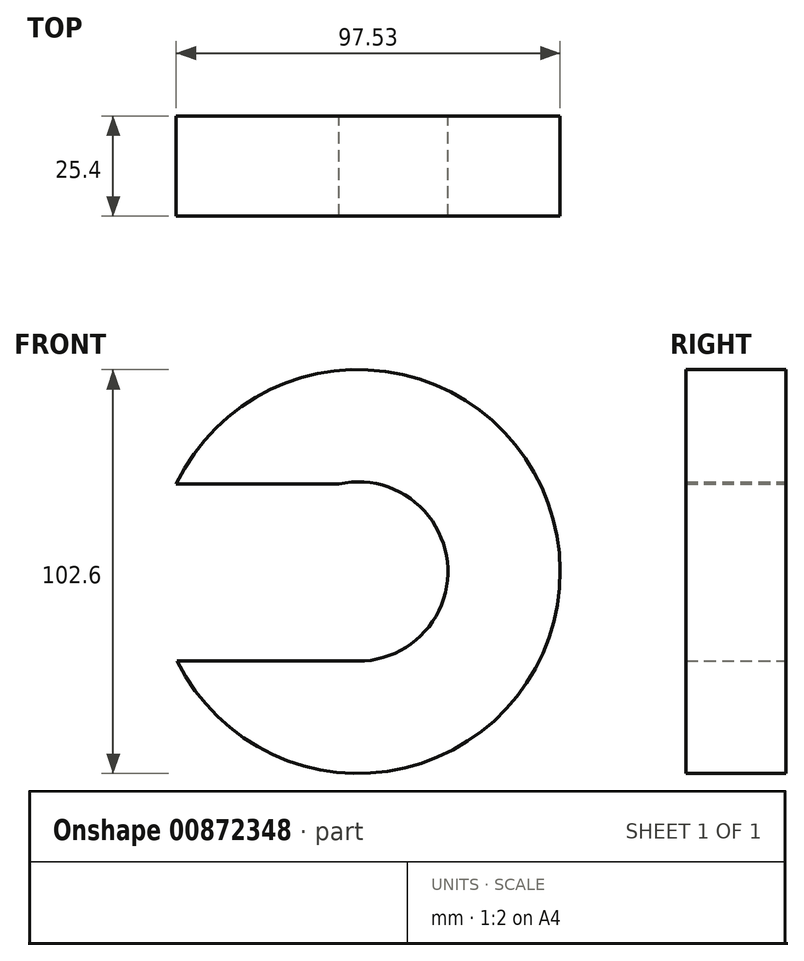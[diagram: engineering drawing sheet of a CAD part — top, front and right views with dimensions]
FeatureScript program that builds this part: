
annotation { "Feature Type Name" : "Feature", "Feature Type Description" : "" }
export const myFeature = defineFeature(function(context is Context, id is Id, definition is map)
    precondition{}
    {
        {
            var Q0;
            Q0=qCreatedBy(makeId("Front.planeOp"),FACE);
            var sketch = newSketch(context, id + "F0", { "sketchPlane" : qUnion([Q0])});
            skCircle(sketch, "E0", {"center": v(0, 0) * mm, "radius": 51.3 * mm});
            skCircle(sketch, "E1", {"center": v(0, 0) * mm, "radius": 22.78 * mm});
            skLineSegment(sketch, "E2.bottom", {"start": v(0, -22.78) * mm, "end": v(-46.23, -22.78) * mm});
            skLineSegment(sketch, "E2.top", {"start": v(0, 22.25) * mm, "end": v(-46.23, 22.25) * mm});
            skLineSegment(sketch, "E2.left", {"start": v(0, -22.78) * mm, "end": v(0, 22.25) * mm});
            skLineSegment(sketch, "E2.right", {"start": v(-46.23, -22.78) * mm, "end": v(-46.23, 22.25) * mm});
            skSolve(sketch);
        }
        {
            var Q0;
            {var subQ1=sQuery(id+"F0.wireOp",EDGE,"E0");var subQ3=sQuery(id+"F0.wireOp",EDGE,"E2.bottom");var subQ4=makeQuery(id+"F0.imprint","INTERSECT",VERTEX,{"derivedFrom":[subQ1,subQ3]});Q0=makeQuery(id+"F0.imprint","IMPRINT",FACE,{"disambiguationData":[TD([[makeQuery(id+"F0.imprint","IMPRINT",EDGE,{"disambiguationData":[TD([[subQ4,-1.0]])],"derivedFrom":subQ1}),1.0]])]});}
            extrude(context, id + "F1", {"entities" : qUnion([Q0]), "depth" : 25.4 * mm, "offsetDistance" : 25.4 * mm});
        }
    });
